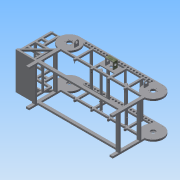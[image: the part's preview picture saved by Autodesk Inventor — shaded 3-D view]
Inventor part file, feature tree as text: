
AUTODESK INVENTOR PART (.ipt)
format: ipt  version: 2015 (Build 190159000, 159)  size: 1,159,680 bytes
history: native  units: mm
features: sketch x44, extrude x43, thread x24, pattern_linear x17, chamfer x5, pattern_circular x2, plane x1, mirror x1, fillet x1, other x1, revolve x1
ambient origin geometry x8: Origin, YZ Plane, XZ Plane, XY Plane, X Axis, Y Axis, Z Axis, Center Point
bodies: 实体1 (feature_tree)
feature tree (140):
  extrude  "拉伸1"  Depth=71.718742mm
  extrude  "拉伸2"  Depth=100.0mm
  extrude  "拉伸5"  Depth=20.0mm
  pattern_linear  "矩形阵列2"  Count1=4  [1 undecoded]
  extrude  "拉伸6"  Depth=12.0mm
  pattern_linear  "矩形阵列14"  Count1=15  [1 undecoded]
  extrude  "拉伸9"  Depth=27.5mm
  pattern_linear  "矩形阵列15"  Count1=140  [1 undecoded]
  extrude  "拉伸10"  Depth=30.0mm
  pattern_linear  "矩形阵列16"  Count1=5  [1 undecoded]
  pattern_linear  "矩形阵列17"  Count1=140  [1 undecoded]
  extrude  "拉伸11"  Depth=40.0mm
  extrude  "拉伸12"  Depth=20.0mm
  thread  "螺纹5"  [1 undecoded]
  pattern_circular  "环形阵列3"  Count=70  [1 undecoded]
  extrude  "拉伸13"  Depth=30.0mm TaperAngle=0.0deg
  extrude  "拉伸14"  Depth=500.0mm
  extrude  "拉伸15"  Depth=30.0mm TaperAngle=0.0deg
  pattern_linear  "矩形阵列18"  Count1=2  [1 undecoded]
  extrude  "拉伸16"  Depth=100.0mm
  thread  "螺纹6"  [1 undecoded]
  thread  "螺纹7"  [1 undecoded]
  thread  "螺纹8"  [1 undecoded]
  thread  "螺纹9"  [1 undecoded]
  pattern_linear  "矩形阵列19"  Count1=4  [1 undecoded]
  pattern_linear  "矩形阵列20"  Count1=2  [1 undecoded]
  pattern_linear  "矩形阵列21"  Count1=8  [1 undecoded]
  extrude  "拉伸17"  Depth=80.0mm
  extrude  "拉伸18"  Depth=55.0mm
  thread  "螺纹10"  [1 undecoded]
  chamfer  "倒角1"  Distance=30.0mm
  plane  "工作平面1"
  mirror  "镜像1"
  pattern_linear  "矩形阵列22"  Count1=6 Spacing1=360.0deg
  extrude  "拉伸19"  Depth=18.0mm TaperAngle=0.0deg
  thread  "螺纹11"  [1 undecoded]
  thread  "螺纹12"  [1 undecoded]
  pattern_circular  "环形阵列4"  Count=4  [1 undecoded]
  extrude  "拉伸20"  Depth=20.0mm
  thread  "螺纹13"  [1 undecoded]
  thread  "螺纹14"  [1 undecoded]
  pattern_linear  "矩形阵列23"  Count1=2 Spacing1=1145.0mm
  extrude  "拉伸21"  Depth=60.0mm
  thread  "螺纹15"  [1 undecoded]
  thread  "螺纹16"  [1 undecoded]
  thread  "螺纹17"  [1 undecoded]
  thread  "螺纹18"  [1 undecoded]
  thread  "螺纹19"  [1 undecoded]
  thread  "螺纹20"  [1 undecoded]
  extrude  "拉伸22"  Depth=5.0mm
  extrude  "拉伸23"  Depth=10.0mm
  pattern_linear  "矩形阵列24"  Count1=6 Spacing1=30.10693mm
  extrude  "拉伸24"  Depth=11.0mm
  pattern_linear  "矩形阵列25"  Count1=5  [1 undecoded]
  extrude  "拉伸25"  Depth=2.0mm
  extrude  "拉伸26"  Depth=2.0mm
  extrude  "拉伸27"  Depth=2.0mm
  extrude  "拉伸28"  Depth=2.0mm
  extrude  "拉伸29"  Depth=2.0mm
  pattern_linear  "矩形阵列26"  Count1=2  [1 undecoded]
  pattern_linear  "矩形阵列27"  Spacing1=13.0mm  [1 undecoded]
  extrude  "拉伸30"  Depth=2.0mm
  extrude  "拉伸31"  Depth=2.0mm
  extrude  "拉伸33"  Depth=2.0mm
  thread  "螺纹21"  [1 undecoded]
  thread  "螺纹22"  [1 undecoded]
  thread  "螺纹23"  [1 undecoded]
  thread  "螺纹24"  [1 undecoded]
  chamfer  "倒角2"  Distance=113.75mm
  extrude  "拉伸34"  Depth=2.0mm
  fillet  "圆角2"  Radius=13.0mm
  extrude  "拉伸35"  Depth=2.0mm
  pattern_linear  "矩形阵列28"  Spacing1=22.0mm  [1 undecoded]
  extrude  "拉伸36"  Depth=10.0mm TaperAngle=0.0deg
  extrude  "拉伸37"  Depth=10.0mm TaperAngle=0.0deg
  extrude  "拉伸38"  Depth=10.0mm TaperAngle=0.0deg
  extrude  "拉伸39"  Depth=10.0mm TaperAngle=0.0deg
  extrude  "拉伸40"  Depth=10.0mm TaperAngle=0.0deg
  extrude  "拉伸41"  Depth=10.0mm TaperAngle=0.0deg
  extrude  "拉伸42"  Depth=325.0mm
  chamfer  "倒角3"  Distance=30.0mm
  sketch  "草图44"  dims[d233=10.0mm]
  other  "工作轴1"
  revolve  "旋转1"  [1 undecoded]
  extrude  "拉伸43"  TaperAngle=135.0deg  [1 undecoded]
  extrude  "拉伸44"  Depth=30.0mm
  extrude  "拉伸45"  Depth=30.0mm TaperAngle=0.0deg
  extrude  "拉伸46"  Depth=20.0mm
  pattern_linear  "矩形阵列29"  Count1=28  [1 undecoded]
  extrude  "拉伸47"  Depth=300.0mm
  thread  "螺纹25"  [1 undecoded]
  thread  "螺纹26"  [1 undecoded]
  chamfer  "倒角4"  Distance=30.0mm
  extrude  "拉伸48"  Depth=30.0mm
  thread  "螺纹27"  [1 undecoded]
  thread  "螺纹28"  [1 undecoded]
  chamfer  "倒角5"  Distance=30.0mm
  sketch  "草图1"  dims[d0=76.775194mm d1=71.718742mm]
  sketch  "草图2"  dims[d2=25.0mm d3=100.0mm]
  sketch  "草图5"  dims[d4=60.0mm d6=180.0deg d8=20.0mm d9=40.0mm]
  sketch  "草图6"  dims[d11=12.0mm d12=12.0mm]
  sketch  "草图9"  dims[d13=20.683537mm]
  sketch  "草图10"  dims[d14=25.0mm]
  sketch  "草图11"  dims[d15=35.0mm d16=150.0mm]
  sketch  "草图12"  dims[d17=40.0mm d18=27.5mm d19=1400.0mm]
  sketch  "草图13"  dims[d20=230.0mm d22=50.0mm d23=10.0mm d25=10.0mm d27=30.0mm]
  sketch  "草图14"  dims[d28=265.0mm d29=50.0mm d32=1400.0mm]
  sketch  "草图15"  dims[d33=25.0mm d34=40.0mm d36=280.0mm d37=10.0mm d39=10.0mm]
  sketch  "草图16"  dims[d41=30.0mm d42=0.0mm d43=20.0mm d45=1400.0mm d46=10.0mm d48=10.0mm d50=30.0mm d51=0.0mm d67=700.0mm]
  sketch  "草图17"  dims[d68=50.0mm d69=30.0mm d70=0.0mm]
  sketch  "草图18"  dims[d71=20.0mm d73=1400.0mm d74=500.0mm]
  sketch  "草图19"  dims[d75=50.0mm d76=30.0mm d77=0.0mm d135=20.0mm d137=590.0mm]
  sketch  "草图20"  dims[d138=30.0mm d139=100.0mm d140=50.0mm d141=0.0mm d142=20.0mm d144=1400.0mm d145=30.0mm d146=590.0mm d147=0.0mm d148=40.0mm d150=280.0mm d151=20.0mm d153=350.0mm d154=80.0mm]
  sketch  "草图21"  dims[d155=30.0mm d156=0.0mm d157=80.0mm]
  sketch  "草图22"  dims[d158=25.0mm d159=55.0mm d160=8.0mm d161=30.0mm d162=0.0mm]
  sketch  "草图23"  dims[d163=10.0mm d164=0.0mm d165=60.0mm d166=360.0deg]
  sketch  "草图25"  dims[d168=80.0mm d169=18.0mm d170=0.0mm d171=62.0mm d172=5.0mm d173=0.0mm d174=40.0mm]
  sketch  "草图26"  dims[d175=5.0mm d176=0.0mm d177=20.0mm d179=1400.0mm d180=4.0mm d181=4.0mm]
  sketch  "草图27"  dims[d182=22.5mm]
  sketch  "草图28"  dims[d183=22.5mm]
  sketch  "草图29"  dims[d184=22.5mm]
  sketch  "草图30"  dims[d185=22.5mm]
  sketch  "草图31"  dims[d186=5.0mm d187=0.0mm]
  sketch  "草图32"  dims[d188=10.0mm d189=0.0mm]
  sketch  "草图34"  dims[d190=10.0mm d191=0.0mm]
  sketch  "草图35"  dims[d192=10.0mm d193=0.0mm]
  sketch  "草图36"  dims[d194=10.0mm d195=0.0mm d196=20.0mm d198=1145.0mm]
  sketch  "草图37"  dims[d199=20.0mm d201=197.5mm d202=60.0mm d204=150.0mm d205=20.0mm d206=5.0mm d207=0.0mm d208=10.0mm d209=28.0mm d210=0.0mm d211=10.0mm d212=0.0mm d213=0.25mm d214=2.0mm d215=45.0deg]
  sketch  "草图38"  dims[d216=40.0mm d218=280.0mm d219=5.0mm]
  sketch  "草图39"  dims[d220=153.0mm d221=10.0mm]
  sketch  "草图40"  dims[d222=28.0mm d223=0.0mm]
  sketch  "草图41"  dims[d224=10.0mm d225=0.0mm]
  sketch  "草图42"  dims[d226=10.0mm d227=0.0mm d228=60.0mm d229=30.10693mm]
  sketch  "草图43"  dims[d231=8.0mm d232=11.0mm]
  sketch  "草图45"  dims[d234=8.0mm]
  sketch  "草图46"  dims[d235=11.0mm]
  sketch  "草图47"  dims[d236=10.0mm]
  sketch  "草图48"  dims[d237=22.0mm d238=0.0mm]
  sketch  "草图49"  dims[d239=10.0mm d240=0.0mm]
  sketch  "草图50"  dims[d241=10.0mm d242=0.0mm d243=50.0mm d245=220.0mm d246=8.0mm d247=8.0mm d248=8.0mm d249=8.0mm d252=8.0mm d253=20.0mm d254=13.0mm d255=13.0mm d256=113.75mm d257=8.0mm d258=13.0mm d259=207.5mm d260=20.0mm d261=13.0mm d262=113.75mm d263=207.5mm d264=13.0mm d265=13.0mm d266=22.0mm d267=0.0mm d268=10.0mm d269=0.0mm d270=10.0mm d271=0.0mm d272=10.0mm d273=0.0mm d274=10.0mm d275=0.0mm d276=10.0mm d277=0.0mm d278=10.0mm d279=0.0mm d280=325.0mm d281=30.0mm d282=10.0mm d283=0.0mm d284=135.0deg d285=30.0mm d286=30.0mm d287=0.0mm d288=20.0mm d290=590.0mm d291=280.0mm d292=300.0mm d293=150.0mm d294=280.0mm d295=30.0mm d296=30.0mm d297=30.0mm d298=30.0mm d299=30.0mm d300=30.0mm d301=30.0mm d302=30.0mm d303=30.0mm d304=150.0mm d305=105.0mm d306=30.0mm d307=0.0mm d308=20.0mm d310=530.0mm d311=30.0mm d312=0.0mm d313=15.0mm d314=30.0mm d315=0.0mm d316=15.0mm d317=10.0mm d318=10.0mm d319=30.0mm d320=0.0mm d321=15.0mm d322=30.0mm d323=0.0mm d324=10.0mm d325=10.0mm d326=0.0mm d327=20.0mm d329=490.0mm d330=20.0mm d332=150.0mm d333=120.0mm d334=180.0mm d335=30.0mm d336=30.0mm d337=30.0mm d338=30.0mm d339=0.0mm d340=15.0mm d341=15.0mm d342=15.0mm d343=15.0mm d344=10.0mm d345=0.0mm d360=30.0mm d361=10.0mm d362=10.0mm d363=10.0mm d364=10.0mm d365=15.0mm d366=15.0mm d367=15.0mm d368=15.0mm d369=15.0mm d370=15.0mm d371=15.0mm d372=15.0mm d373=20.0mm d374=0.0mm d375=10.0mm d376=0.0mm d377=10.0mm d378=0.0mm d379=10.0mm d380=0.0mm d381=10.0mm d382=0.0mm d383=0.5mm d384=2.0mm d385=45.0deg d386=70.0mm d387=14.0mm d388=110.0mm d389=99.418mm d390=0.0mm d391=35.0mm d392=42.0mm d393=42.0mm d394=0.0mm d395=20.0mm d397=1166.0mm d398=140.0mm d399=70.0mm d400=14.0mm d401=0.0mm d402=630.0mm d403=140.0mm d404=70.0mm d405=35.0mm d406=116.414mm d407=0.0mm d408=14.0mm d409=14.0mm d410=14.0mm d411=70.0mm d412=0.0mm d413=140.0mm d414=0.0mm d415=42.0mm d416=700.0mm d417=0.0mm d418=14.0mm d419=0.0mm d420=27.0mm d421=5.0mm d422=0.0mm d423=20.0mm d424=18.378mm d425=0.0mm d426=0.5mm d427=2.0mm d428=45.0deg d429=1.2mm d430=4.0mm d431=79.175mm d432=5.178742mm d433=90.0deg d434=20.0mm d435=20.0mm d436=30.0mm d437=30.0mm d438=210.0mm d439=160.0mm d440=10.0mm d441=0.0mm d442=230.0mm d443=10.0mm d444=0.0mm d445=30.0mm d446=0.0mm d447=60.0mm d448=60.0mm d449=30.0mm d450=0.0mm d451=20.0mm d453=590.0mm d454=10.0mm d455=15.0mm d456=20.0mm d457=10.0mm d458=15.0mm d459=429.5mm d460=20.0mm d461=0.0mm d462=10.0mm d463=0.0mm d464=10.0mm d465=0.0mm d466=1.0mm d467=2.0mm d468=45.0deg d469=10.0mm d470=10.0mm d471=15.0mm d472=20.0mm d473=15.0mm d474=429.5mm d475=20.0mm d476=0.0mm d477=10.0mm d478=0.0mm d479=10.0mm d480=0.0mm d481=1.0mm d482=2.0mm d483=45.0deg]
note: 42 required parameter values undecoded (feature->parameter linkage not recoverable at this tier; creation-order binding heuristic only, values carry confidence <= 0.55)